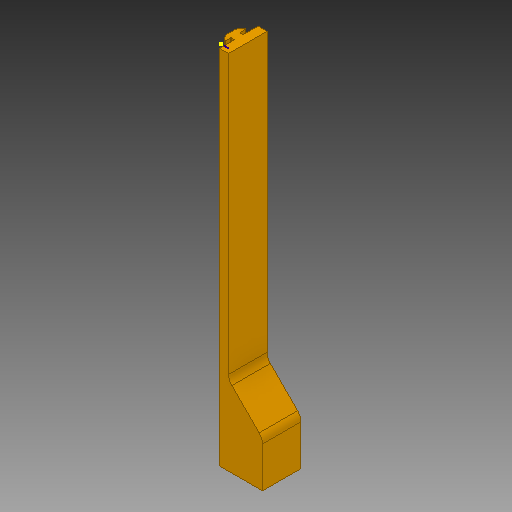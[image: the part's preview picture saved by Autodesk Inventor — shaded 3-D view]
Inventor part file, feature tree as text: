
AUTODESK INVENTOR PART (.ipt)
format: ipt  version: 2019 (Build 230136000, 136)  size: 211,456 bytes
history: native  units: in
note: dims shown in document units (in); Inventor stores cm internally (conversion verified against a paired STEP export)
features: sketch x7, extrude x6, fillet x3, other x1, plane x1, chamfer x1
ambient origin geometry x8: Origin, YZ Plane, XZ Plane, XY Plane, X Axis, Y Axis, Z Axis, Center Point
bodies: Solid1 (feature_tree)
feature tree (19):
  other  "20X20Connector"
  extrude  "Extrusion1"  Depth=1.0in
  plane  "Work Plane1"
  fillet  "Fillet2"  Radius=1.0in
  extrude  "Extrusion2"  Depth=7.0in TaperAngle=0.0deg
  sketch  "Sketch3"  dims[d22=0.1in d23=0.0in d24=0.0156in d25=1.0in]
  extrude  "Extrusion3"  Depth=0.0156in
  fillet  "Fillet3"  Radius=1.0in
  extrude  "Extrusion4"  Depth=0.75in TaperAngle=45.0deg
  chamfer  "Chamfer1"  Distance=0.1in
  extrude  "Extrusion5"  Depth=0.25in
  extrude  "Extrusion6"  [1 undecoded]
  fillet  "Fillet4"  [1 undecoded]
  sketch  "Sketch1"  dims[d0=0.0984in d1=0.0787in d2=0.1874in d3=0.4524in d4=0.1085in d5=0.225in d6=0.2221in d7=0.2313in d8=0.03in d9=0.03in d11=0.9949in d12=0.1137in d13=0.6693in d14=0.65in d15=1.0in d16=0.0in]
  sketch  "Sketch2"  dims[d17=0.0in d19=0.0156in d20=7.0in d21=0.0in]
  sketch  "Sketch4"  dims[d26=0.75in d27=0.0in d28=0.75in d29=0.125in d30=45.0deg d31=0.1in d32=0.0in]
  sketch  "Sketch5"  dims[d33=0.1in d34=0.0in d35=0.25in]
  sketch  "Sketch6"
  sketch  "Sketch7"
note: 2 required parameter values undecoded (feature->parameter linkage not recoverable at this tier; creation-order binding heuristic only, values carry confidence <= 0.55)
